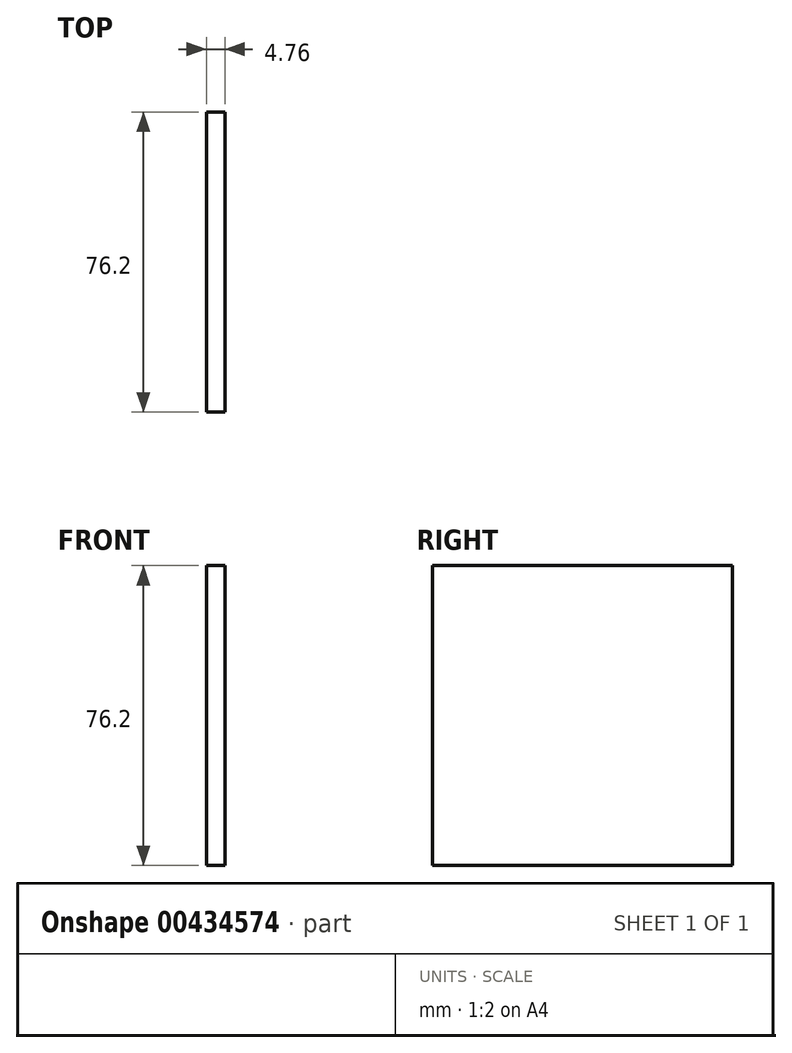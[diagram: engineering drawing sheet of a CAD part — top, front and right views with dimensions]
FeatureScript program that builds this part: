
annotation { "Feature Type Name" : "Feature", "Feature Type Description" : "" }
export const myFeature = defineFeature(function(context is Context, id is Id, definition is map)
    precondition{}
    {
        {
            var Q0;
            Q0=qCreatedBy(makeId("Right.planeOp"),FACE);
            var sketch = newSketch(context, id + "F0", { "sketchPlane" : qUnion([Q0])});
            skLineSegment(sketch, "E0.bottom", {"start": v(-53.68, 71.23) * mm, "end": v(22.52, 71.23) * mm});
            skLineSegment(sketch, "E0.top", {"start": v(-53.68, -4.97) * mm, "end": v(22.52, -4.97) * mm});
            skLineSegment(sketch, "E0.left", {"start": v(-53.68, 71.23) * mm, "end": v(-53.68, -4.97) * mm});
            skLineSegment(sketch, "E0.right", {"start": v(22.52, 71.23) * mm, "end": v(22.52, -4.97) * mm});
            skSolve(sketch);
        }
        {
            var Q0;
            Q0=makeQuery(id+"F0.imprint","IMPRINT",FACE,{"disambiguationData":[TD([[makeQuery(id+"F0.imprint","IMPRINT",EDGE,{"derivedFrom":sQuery(id+"F0.wireOp",EDGE,"E0.bottom")}),-1.0]])]});
            extrude(context, id + "F1", {"entities" : qUnion([Q0]), "depth" : 4.76 * mm});
        }
    });
